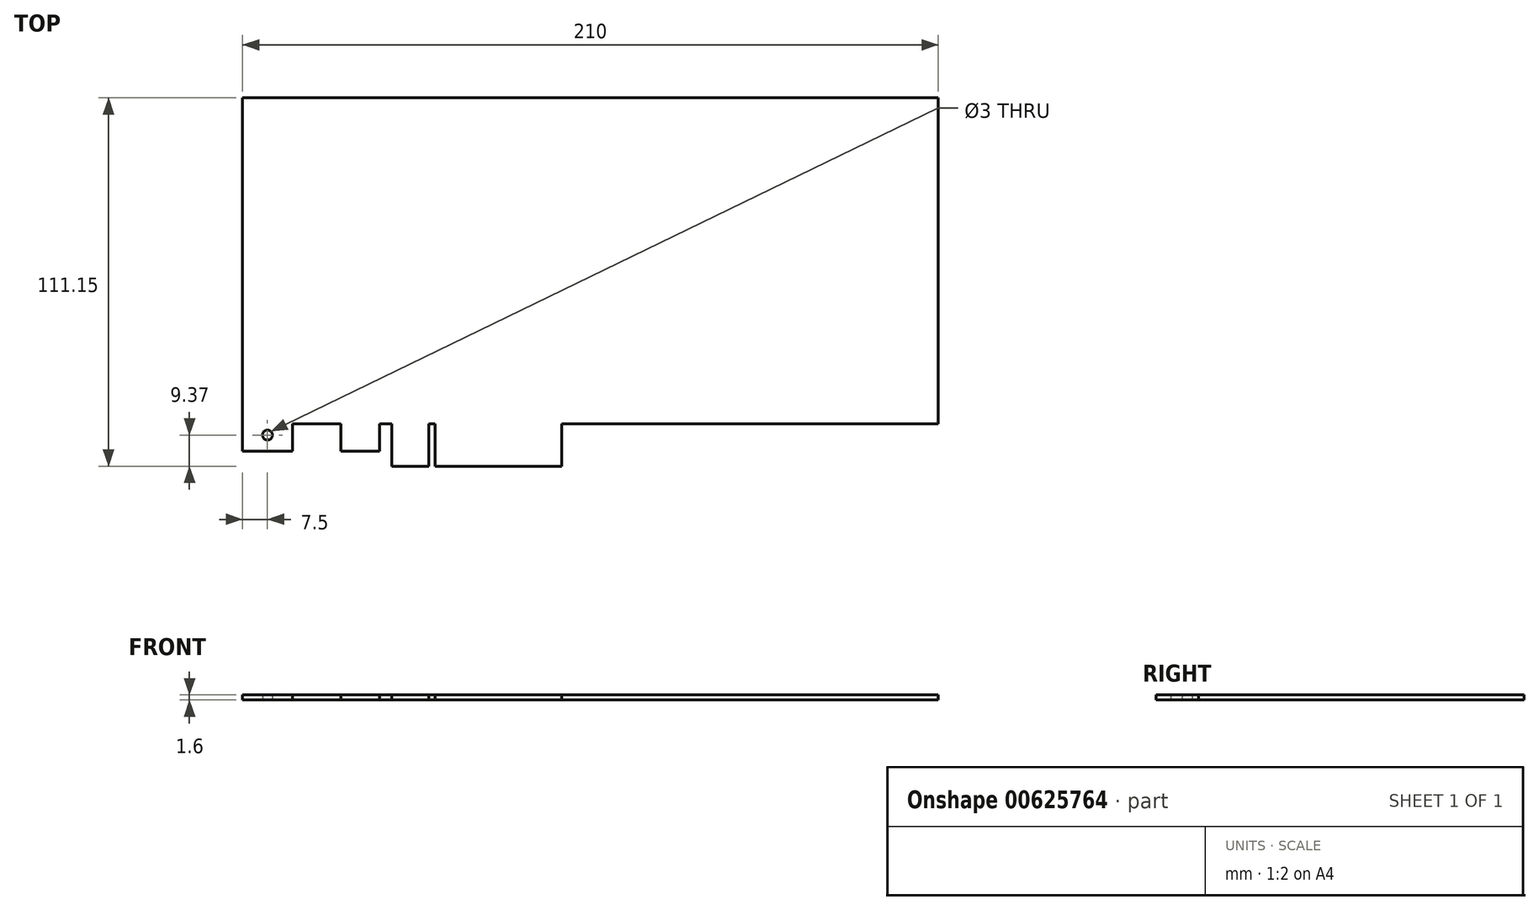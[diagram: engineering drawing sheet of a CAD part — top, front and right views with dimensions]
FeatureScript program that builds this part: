
annotation { "Feature Type Name" : "Feature", "Feature Type Description" : "" }
export const myFeature = defineFeature(function(context is Context, id is Id, definition is map)
    precondition{}
    {
        {
            var Q0;
            Q0=qCreatedBy(makeId("Top.planeOp"),FACE);
            var sketch = newSketch(context, id + "F0", { "sketchPlane" : qUnion([Q0])});
            skLineSegment(sketch, "E0", {"start": v(210, 106.65) * mm, "end": v(210, 8.27) * mm});
            skLineSegment(sketch, "E1", {"start": v(210, 8.27) * mm, "end": v(96.3, 8.27) * mm});
            skLineSegment(sketch, "E2", {"start": v(96.3, 8.27) * mm, "end": v(96.3, -4.5) * mm});
            skLineSegment(sketch, "E3", {"start": v(58.1, -4.5) * mm, "end": v(58.1, 8.27) * mm});
            skLineSegment(sketch, "E4", {"start": v(58.1, 8.27) * mm, "end": v(56.2, 8.27) * mm});
            skLineSegment(sketch, "E5", {"start": v(56.2, 8.27) * mm, "end": v(56.2, -4.5) * mm});
            skLineSegment(sketch, "E6", {"start": v(56.2, -4.5) * mm, "end": v(45, -4.5) * mm});
            skLineSegment(sketch, "E7", {"start": v(45, -4.5) * mm, "end": v(45, 8.25) * mm});
            skLineSegment(sketch, "E8", {"start": v(45, 8.25) * mm, "end": v(41.35, 8.25) * mm});
            skLineSegment(sketch, "E9", {"start": v(41.35, 8.25) * mm, "end": v(41.35, 0) * mm});
            skLineSegment(sketch, "E10", {"start": v(41.35, 0) * mm, "end": v(29.7, 0) * mm});
            skLineSegment(sketch, "E11", {"start": v(29.7, 0) * mm, "end": v(29.7, 8.25) * mm});
            skLineSegment(sketch, "E12", {"start": v(29.7, 8.25) * mm, "end": v(15, 8.25) * mm});
            skLineSegment(sketch, "E13", {"start": v(15, 8.25) * mm, "end": v(15, 0) * mm});
            skLineSegment(sketch, "E14", {"start": v(15, 0) * mm, "end": v(0, 0) * mm});
            skLineSegment(sketch, "E15", {"start": v(0, 0) * mm, "end": v(0, 106.65) * mm});
            skLineSegment(sketch, "E16", {"start": v(0, 106.65) * mm, "end": v(210, 106.65) * mm});
            skLineSegment(sketch, "E17", {"start": v(57.15, 8.27) * mm, "end": v(57.15, -21.08) * mm, "construction": true});
            skLineSegment(sketch, "E18", {"start": v(96.3, -4.5) * mm, "end": v(58.1, -4.5) * mm});
            skCircle(sketch, "E19", {"center": v(7.5, 4.87) * mm, "radius": 1.5 * mm});
            skSolve(sketch);
        }
        {
            var Q0;
            Q0=makeQuery(id+"F0.imprint","IMPRINT",FACE,{"disambiguationData":[TD([[makeQuery(id+"F0.imprint","IMPRINT",EDGE,{"derivedFrom":sQuery(id+"F0.wireOp",EDGE,"E0")}),-1.0]])]});
            var Q1;
            Q1=sQuery(id+"F0.wireOp",EDGE,"E16");
            var Q2;
            Q2=sQuery(id+"F0.wireOp",EDGE,"E0");
            var Q3;
            Q3=sQuery(id+"F0.wireOp",EDGE,"E1");
            var Q4;
            Q4=sQuery(id+"F0.wireOp",EDGE,"E2");
            var Q5;
            Q5=sQuery(id+"F0.wireOp",EDGE,"E18");
            var Q6;
            Q6=sQuery(id+"F0.wireOp",EDGE,"E15");
            var Q7;
            Q7=sQuery(id+"F0.wireOp",EDGE,"E14");
            var Q8;
            Q8=sQuery(id+"F0.wireOp",EDGE,"E13");
            var Q9;
            Q9=sQuery(id+"F0.wireOp",EDGE,"E12");
            var Q10;
            Q10=sQuery(id+"F0.wireOp",EDGE,"E11");
            var Q11;
            Q11=sQuery(id+"F0.wireOp",EDGE,"E10");
            var Q12;
            Q12=sQuery(id+"F0.wireOp",EDGE,"E9");
            var Q13;
            Q13=sQuery(id+"F0.wireOp",EDGE,"E8");
            var Q14;
            Q14=sQuery(id+"F0.wireOp",EDGE,"E7");
            var Q15;
            Q15=sQuery(id+"F0.wireOp",EDGE,"E5");
            var Q16;
            Q16=sQuery(id+"F0.wireOp",EDGE,"E4");
            var Q17;
            Q17=sQuery(id+"F0.wireOp",EDGE,"E3");
            extrude(context, id + "F1", {"entities" : qUnion([Q0]), "surfaceEntities" : qUnion([Q1, Q2, Q3, Q4, Q5, Q6, Q7, Q8, Q9, Q10, Q11, Q12, Q13, Q14, Q15, Q16, Q17]), "depth" : 1.6 * mm, "offsetDistance" : 25 * mm});
        }
    });
